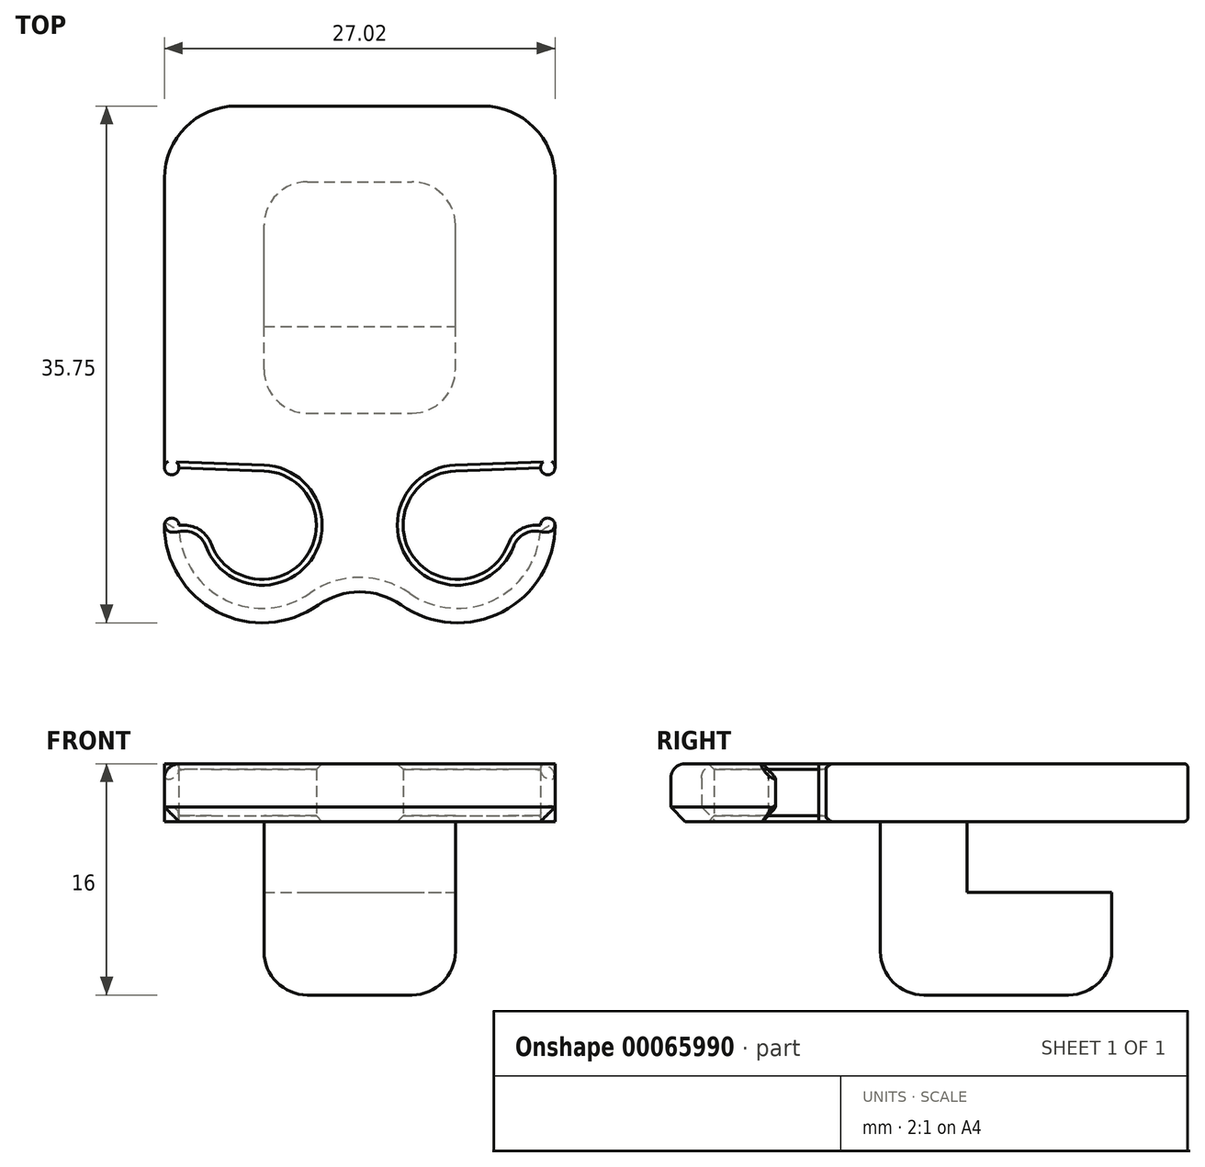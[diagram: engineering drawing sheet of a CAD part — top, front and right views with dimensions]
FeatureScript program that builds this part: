
annotation { "Feature Type Name" : "Feature", "Feature Type Description" : "" }
export const myFeature = defineFeature(function(context is Context, id is Id, definition is map)
    precondition{}
    {
        {
            var Q0;
            Q0=qCreatedBy(makeId("Top.planeOp"),FACE);
            var sketch = newSketch(context, id + "F0", { "sketchPlane" : qUnion([Q0])});
            skPoint(sketch, "E0.0", {"position": v(0, 0) * mm});
            skLineSegment(sketch, "E1.bottom", {"start": v(0, 0) * mm, "end": v(-3, 0) * mm, "construction": true});
            skLineSegment(sketch, "E1.top", {"start": v(0, 29) * mm, "end": v(-8.5, 29) * mm});
            skLineSegment(sketch, "E1.left", {"start": v(0, 0) * mm, "end": v(0, 29) * mm, "construction": true});
            skLineSegment(sketch, "E1.right", {"start": v(-13.5, 4) * mm, "end": v(-13.5, 24) * mm});
            skArc(sketch, "E2", {"start": v(-13.5, 0) * mm, "mid": v(-9.87, -6) * mm, "end": v(-2.87, -5.53) * mm});
            skArc(sketch, "E3", {"start": v(-10.27, -1.3) * mm, "mid": v(-3.71, -2.2) * mm, "end": v(-6.62, 3.75) * mm});
            skLineSegment(sketch, "E4", {"start": v(-6.62, 3.75) * mm, "end": v(-12.5, 3.96) * mm});
            skLineSegment(sketch, "E5.trimOffspring", {"start": v(-12.15, 0) * mm, "end": v(-12.5, 0) * mm});
            skLineSegment(sketch, "E6.MirrorCS", {"start": v(0, 0) * mm, "end": v(3, 0) * mm, "construction": true});
            skArc(sketch, "E7.MirrorCS", {"start": v(13.5, 0) * mm, "mid": v(9.87, -6) * mm, "end": v(2.87, -5.53) * mm});
            skArc(sketch, "E8.MirrorCS", {"start": v(10.27, -1.3) * mm, "mid": v(3.71, -2.2) * mm, "end": v(6.62, 3.75) * mm});
            skLineSegment(sketch, "E9.MirrorCS", {"start": v(13.5, 4) * mm, "end": v(13.5, 24) * mm});
            skLineSegment(sketch, "E10.MirrorCS", {"start": v(6.62, 3.75) * mm, "end": v(12.5, 3.96) * mm});
            skLineSegment(sketch, "E11.MirrorCS", {"start": v(0, 29) * mm, "end": v(8.5, 29) * mm});
            skLineSegment(sketch, "E12.MirrorCS", {"start": v(12.15, 0) * mm, "end": v(12.5, 0) * mm});
            skArc(sketch, "E13.filletArc", {"start": v(2.87, -5.53) * mm, "mid": v(0, -4.62) * mm, "end": v(-2.87, -5.53) * mm});
            skPoint(sketch, "E14.visualSharp", {"position": v(-13.5, 29) * mm});
            skArc(sketch, "E14.filletArc", {"start": v(-8.5, 29) * mm, "mid": v(-12.04, 27.54) * mm, "end": v(-13.5, 24) * mm});
            skPoint(sketch, "E15.visualSharp", {"position": v(13.5, 29) * mm});
            skArc(sketch, "E15.filletArc", {"start": v(13.5, 24) * mm, "mid": v(12.04, 27.54) * mm, "end": v(8.5, 29) * mm});
            skLineSegment(sketch, "E16", {"start": v(-10.06, 3.87) * mm, "end": v(-10.06, 28.75) * mm, "construction": true});
            skArc(sketch, "E17", {"start": v(-13.5, 4) * mm, "mid": v(-13.02, 3.48) * mm, "end": v(-12.5, 3.96) * mm});
            skArc(sketch, "E18", {"start": v(-12.5, 0) * mm, "mid": v(-13, 0.5) * mm, "end": v(-13.5, 0) * mm});
            skArc(sketch, "E19.MirrorC", {"start": v(13.5, 4) * mm, "mid": v(13.02, 3.48) * mm, "end": v(12.5, 3.96) * mm});
            skArc(sketch, "E20.MirrorC", {"start": v(12.5, 0) * mm, "mid": v(13, 0.5) * mm, "end": v(13.5, 0) * mm});
            skPoint(sketch, "E21.visualSharp", {"position": v(10.5, 0) * mm});
            skArc(sketch, "E21.filletArc", {"start": v(12.15, 0) * mm, "mid": v(11, -0.36) * mm, "end": v(10.27, -1.3) * mm});
            skPoint(sketch, "E22.visualSharp", {"position": v(-10.5, 0) * mm});
            skArc(sketch, "E22.filletArc", {"start": v(-10.27, -1.3) * mm, "mid": v(-11, -0.36) * mm, "end": v(-12.15, 0) * mm});
            skSolve(sketch);
        }
        {
            var Q0;
            Q0=makeQuery(id+"F0.imprint","IMPRINT",FACE,{"disambiguationData":[TD([[makeQuery(id+"F0.imprint","IMPRINT",EDGE,{"derivedFrom":sQuery(id+"F0.wireOp",EDGE,"E1.top")}),1.0]])]});
            extrude(context, id + "F1", {"entities" : qUnion([Q0]), "depth" : 4 * mm});
        }
        {
            var Q0;
            Q0=makeQuery(id+"F1.opExtrude","CAP_FACE",FACE,{"disambiguationData":[OSD([sQuery(id+"F0.wireOp",EDGE,"E1.top"),sQuery(id+"F0.wireOp",EDGE,"E1.right"),sQuery(id+"F0.wireOp",EDGE,"E2"),sQuery(id+"F0.wireOp",EDGE,"E3"),sQuery(id+"F0.wireOp",EDGE,"E4"),sQuery(id+"F0.wireOp",EDGE,"E5.trimOffspring"),sQuery(id+"F0.wireOp",EDGE,"E7.MirrorCS"),sQuery(id+"F0.wireOp",EDGE,"E8.MirrorCS"),sQuery(id+"F0.wireOp",EDGE,"E9.MirrorCS"),sQuery(id+"F0.wireOp",EDGE,"E10.MirrorCS"),sQuery(id+"F0.wireOp",EDGE,"E11.MirrorCS"),sQuery(id+"F0.wireOp",EDGE,"E12.MirrorCS"),sQuery(id+"F0.wireOp",EDGE,"E13.filletArc"),sQuery(id+"F0.wireOp",EDGE,"E14.filletArc"),sQuery(id+"F0.wireOp",EDGE,"E15.filletArc"),sQuery(id+"F0.wireOp",EDGE,"E17"),sQuery(id+"F0.wireOp",EDGE,"E18"),sQuery(id+"F0.wireOp",EDGE,"E19.MirrorC"),sQuery(id+"F0.wireOp",EDGE,"E20.MirrorC"),sQuery(id+"F0.wireOp",EDGE,"E21.filletArc"),sQuery(id+"F0.wireOp",EDGE,"E22.filletArc")])],"isStart":true});
            var sketch = newSketch(context, id + "F2", { "sketchPlane" : qUnion([Q0])});
            skLineSegment(sketch, "E23.bottom", {"start": v(-6.62, -7.75) * mm, "end": v(6.62, -7.75) * mm});
            skLineSegment(sketch, "E23.top", {"start": v(-6.62, -13.75) * mm, "end": v(6.62, -13.75) * mm});
            skLineSegment(sketch, "E23.left", {"start": v(-6.62, -7.75) * mm, "end": v(-6.62, -13.75) * mm});
            skLineSegment(sketch, "E23.right", {"start": v(6.62, -7.75) * mm, "end": v(6.62, -13.75) * mm});
            skLineSegment(sketch, "E24.top", {"start": v(-6.62, -23.75) * mm, "end": v(6.62, -23.75) * mm});
            skLineSegment(sketch, "E24.left", {"start": v(-6.62, -13.75) * mm, "end": v(-6.62, -23.75) * mm});
            skLineSegment(sketch, "E24.right", {"start": v(6.62, -13.75) * mm, "end": v(6.62, -23.75) * mm});
            skSolve(sketch);
        }
        {
            var Q0;
            Q0=makeQuery(id+"F2.imprint","IMPRINT",FACE,{"disambiguationData":[TD([[makeQuery(id+"F2.imprint","IMPRINT",EDGE,{"derivedFrom":sQuery(id+"F2.wireOp",EDGE,"E23.bottom")}),-1.0]])]});
            var Q1;
            Q1=makeQuery(id+"F2.imprint","IMPRINT",FACE,{"disambiguationData":[TD([[makeQuery(id+"F2.imprint","IMPRINT",EDGE,{"derivedFrom":sQuery(id+"F2.wireOp",EDGE,"E23.top")}),-1.0]])]});
            extrude(context, id + "F3", {"entities" : qUnion([Q0, Q1]), "operationType" : NewBodyOperationType.ADD, "depth" : 12 * mm});
        }
        {
            var Q0;
            Q0=makeQuery(id+"F2.imprint","IMPRINT",FACE,{"disambiguationData":[TD([[makeQuery(id+"F2.imprint","IMPRINT",EDGE,{"derivedFrom":sQuery(id+"F2.wireOp",EDGE,"E23.top")}),-1.0]])]});
            extrude(context, id + "F4", {"entities" : qUnion([Q0]), "operationType" : NewBodyOperationType.REMOVE, "depth" : 4.9 * mm});
        }
        {
            var Q0;
            Q0=makeQuery(id+"F3.opExtrude","CAP_EDGE",EDGE,{"disambiguationData":[OSD([sQuery(id+"F2.wireOp",EDGE,"E23.left"),sQuery(id+"F2.wireOp",EDGE,"E24.left")])],"isStart":false});
            var Q1;
            Q1=makeQuery(id+"F3.opExtrude","CAP_EDGE",EDGE,{"disambiguationData":[OSD([sQuery(id+"F2.wireOp",EDGE,"E23.bottom")])],"isStart":false});
            var Q2;
            Q2=makeQuery(id+"F3.opExtrude","CAP_EDGE",EDGE,{"disambiguationData":[OSD([sQuery(id+"F2.wireOp",EDGE,"E23.right"),sQuery(id+"F2.wireOp",EDGE,"E24.right")])],"isStart":false});
            var Q3;
            Q3=makeQuery(id+"F3.opExtrude","SWEPT_EDGE",EDGE,{"disambiguationData":[OSD([sQuery(id+"F2.wireOp",EDGE,"E23.bottom"),sQuery(id+"F2.wireOp",EDGE,"E23.right")])]});
            var Q4;
            Q4=makeQuery(id+"F3.opExtrude","SWEPT_EDGE",EDGE,{"disambiguationData":[OSD([sQuery(id+"F2.wireOp",EDGE,"E23.bottom"),sQuery(id+"F2.wireOp",EDGE,"E23.left")])]});
            var Q5;
            Q5=makeQuery(id+"F3.opExtrude","SWEPT_EDGE",EDGE,{"disambiguationData":[OSD([sQuery(id+"F2.wireOp",EDGE,"E24.top"),sQuery(id+"F2.wireOp",EDGE,"E24.right")])]});
            var Q6;
            Q6=makeQuery(id+"F3.opExtrude","CAP_EDGE",EDGE,{"disambiguationData":[OSD([sQuery(id+"F2.wireOp",EDGE,"E24.top")])],"isStart":false});
            var Q7;
            Q7=makeQuery(id+"F3.opExtrude","SWEPT_EDGE",EDGE,{"disambiguationData":[OSD([sQuery(id+"F2.wireOp",EDGE,"E24.top"),sQuery(id+"F2.wireOp",EDGE,"E24.left")])]});
            fillet(context, id + "F5", {"entities" : qUnion([Q0, Q1, Q2, Q3, Q4, Q5, Q6, Q7]), "radius" : 3 * mm, "tangentPropagation" : true, "allowEdgeOverflow" : false});
        }
        {
            var Q0;
            Q0=makeQuery(id+"F1.opExtrude","CAP_EDGE",EDGE,{"disambiguationData":[OSD([sQuery(id+"F0.wireOp",EDGE,"E13.filletArc")])],"isStart":false});
            fillet(context, id + "F6", {"entities" : qUnion([Q0]), "radius" : 1 * mm, "tangentPropagation" : true, "allowEdgeOverflow" : false});
        }
        {
            var Q0;
            Q0=makeQuery(id+"F1.opExtrude","CAP_EDGE",EDGE,{"disambiguationData":[OSD([sQuery(id+"F0.wireOp",EDGE,"E13.filletArc")])],"isStart":true});
            chamfer(context, id + "F7", {"entities" : qUnion([Q0]), "width" : 1 * mm, "tangentPropagation" : true});
        }
        {
            var Q0;
            Q0=makeQuery(id+"F1.opExtrude","CAP_EDGE",EDGE,{"disambiguationData":[OSD([sQuery(id+"F0.wireOp",EDGE,"E8.MirrorCS")])],"isStart":false});
            var Q1;
            Q1=makeQuery(id+"F1.opExtrude","CAP_EDGE",EDGE,{"disambiguationData":[OSD([sQuery(id+"F0.wireOp",EDGE,"E3")])],"isStart":true});
            var Q2;
            Q2=makeQuery(id+"F1.opExtrude","CAP_EDGE",EDGE,{"disambiguationData":[OSD([sQuery(id+"F0.wireOp",EDGE,"E3")])],"isStart":false});
            var Q3;
            Q3=makeQuery(id+"F1.opExtrude","CAP_EDGE",EDGE,{"disambiguationData":[OSD([sQuery(id+"F0.wireOp",EDGE,"E8.MirrorCS")])],"isStart":true});
            var Q4;
            Q4=makeQuery(id+"F1.opExtrude","CAP_EDGE",EDGE,{"disambiguationData":[OSD([sQuery(id+"F0.wireOp",EDGE,"E21.filletArc")])],"isStart":false});
            var Q5;
            Q5=makeQuery(id+"F1.opExtrude","CAP_EDGE",EDGE,{"disambiguationData":[OSD([sQuery(id+"F0.wireOp",EDGE,"E22.filletArc")])],"isStart":false});
            var Q6;
            Q6=makeQuery(id+"F1.opExtrude","CAP_EDGE",EDGE,{"disambiguationData":[OSD([sQuery(id+"F0.wireOp",EDGE,"E22.filletArc")])],"isStart":true});
            var Q7;
            Q7=makeQuery(id+"F1.opExtrude","CAP_EDGE",EDGE,{"disambiguationData":[OSD([sQuery(id+"F0.wireOp",EDGE,"E21.filletArc")])],"isStart":true});
            var Q8;
            Q8=makeQuery(id+"F1.opExtrude","CAP_EDGE",EDGE,{"disambiguationData":[OSD([sQuery(id+"F0.wireOp",EDGE,"E10.MirrorCS")])],"isStart":true});
            var Q9;
            Q9=makeQuery(id+"F1.opExtrude","CAP_EDGE",EDGE,{"disambiguationData":[OSD([sQuery(id+"F0.wireOp",EDGE,"E10.MirrorCS")])],"isStart":false});
            var Q10;
            Q10=makeQuery(id+"F1.opExtrude","CAP_EDGE",EDGE,{"disambiguationData":[OSD([sQuery(id+"F0.wireOp",EDGE,"E4")])],"isStart":true});
            var Q11;
            Q11=makeQuery(id+"F1.opExtrude","CAP_EDGE",EDGE,{"disambiguationData":[OSD([sQuery(id+"F0.wireOp",EDGE,"E4")])],"isStart":false});
            chamfer(context, id + "F8", {"entities" : qUnion([Q0, Q1, Q2, Q3, Q4, Q5, Q6, Q7, Q8, Q9, Q10, Q11]), "width" : .4 * mm});
        }
        {
            var Q0;
            Q0=makeQuery(id+"F1.opExtrude","CAP_EDGE",EDGE,{"disambiguationData":[OSD([sQuery(id+"F0.wireOp",EDGE,"E1.right")])],"isStart":false});
            var Q1;
            Q1=makeQuery(id+"F1.opExtrude","CAP_EDGE",EDGE,{"disambiguationData":[OSD([sQuery(id+"F0.wireOp",EDGE,"E1.right")])],"isStart":true});
            var Q2;
            Q2=makeQuery(id+"F1.opExtrude","CAP_EDGE",EDGE,{"disambiguationData":[OSD([sQuery(id+"F0.wireOp",EDGE,"E14.filletArc")])],"isStart":false});
            var Q3;
            Q3=makeQuery(id+"F1.opExtrude","CAP_EDGE",EDGE,{"disambiguationData":[OSD([sQuery(id+"F0.wireOp",EDGE,"E14.filletArc")])],"isStart":true});
            var Q4;
            Q4=makeQuery(id+"F1.opExtrude","CAP_EDGE",EDGE,{"disambiguationData":[OSD([sQuery(id+"F0.wireOp",EDGE,"E1.top"),sQuery(id+"F0.wireOp",EDGE,"E11.MirrorCS")])],"isStart":false});
            var Q5;
            Q5=makeQuery(id+"F1.opExtrude","CAP_EDGE",EDGE,{"disambiguationData":[OSD([sQuery(id+"F0.wireOp",EDGE,"E1.top"),sQuery(id+"F0.wireOp",EDGE,"E11.MirrorCS")])],"isStart":true});
            var Q6;
            Q6=makeQuery(id+"F1.opExtrude","CAP_EDGE",EDGE,{"disambiguationData":[OSD([sQuery(id+"F0.wireOp",EDGE,"E9.MirrorCS")])],"isStart":false});
            var Q7;
            Q7=makeQuery(id+"F1.opExtrude","CAP_EDGE",EDGE,{"disambiguationData":[OSD([sQuery(id+"F0.wireOp",EDGE,"E15.filletArc")])],"isStart":false});
            var Q8;
            Q8=makeQuery(id+"F1.opExtrude","CAP_EDGE",EDGE,{"disambiguationData":[OSD([sQuery(id+"F0.wireOp",EDGE,"E9.MirrorCS")])],"isStart":true});
            var Q9;
            Q9=makeQuery(id+"F1.opExtrude","CAP_EDGE",EDGE,{"disambiguationData":[OSD([sQuery(id+"F0.wireOp",EDGE,"E15.filletArc")])],"isStart":true});
            fillet(context, id + "F9", {"entities" : qUnion([Q0, Q1, Q2, Q3, Q4, Q5, Q6, Q7, Q8, Q9]), "radius" : .25 * mm, "tangentPropagation" : true, "allowEdgeOverflow" : false});
        }
    });
